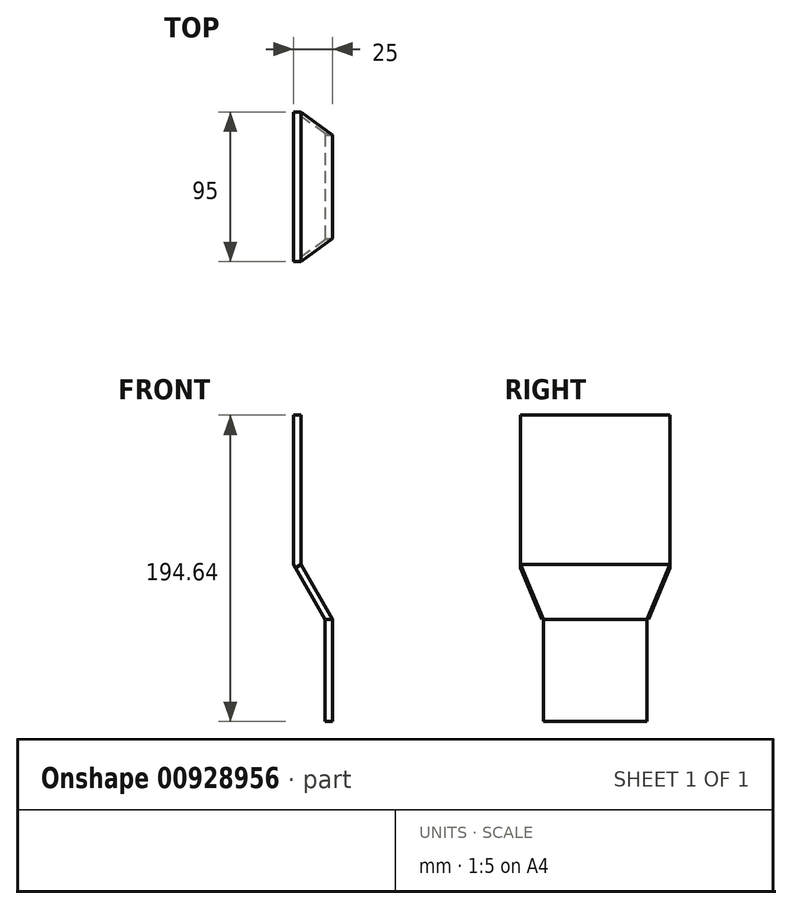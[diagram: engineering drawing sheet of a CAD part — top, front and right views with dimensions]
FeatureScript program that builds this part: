
annotation { "Feature Type Name" : "Feature", "Feature Type Description" : "" }
export const myFeature = defineFeature(function(context is Context, id is Id, definition is map)
    precondition{}
    {
        {
            var Q0;
            Q0=qCreatedBy(makeId("Right.planeOp"),FACE);
            var sketch = newSketch(context, id + "F0", { "sketchPlane" : qUnion([Q0])});
            skLineSegment(sketch, "E0.bottom", {"start": v(-47.5, 47.5) * mm, "end": v(47.5, 47.5) * mm});
            skLineSegment(sketch, "E0.top", {"start": v(-47.5, -47.5) * mm, "end": v(47.5, -47.5) * mm});
            skLineSegment(sketch, "E0.left", {"start": v(-47.5, 47.5) * mm, "end": v(-47.5, -47.5) * mm});
            skLineSegment(sketch, "E0.right", {"start": v(47.5, 47.5) * mm, "end": v(47.5, -47.5) * mm});
            skLineSegment(sketch, "E1", {"start": v(0, 83.18) * mm, "end": v(0, -90.06) * mm, "construction": true});
            skLineSegment(sketch, "E2", {"start": v(-68.56, 0) * mm, "end": v(78.45, 0) * mm, "construction": true});
            skSolve(sketch);
        }
        {
            var Q0;
            Q0 = qSketchRegion(id + "F0", true);
            extrude(context, id + "F1", {"entities" : qUnion([Q0]), "depth" : 5 * mm, "offsetDistance" : 25.4 * mm});
        }
        {
            var Q0;
            Q0=makeQuery(id+"F1.opExtrude","SWEPT_FACE",FACE,{"disambiguationData":[OSD([sQuery(id+"F0.wireOp",EDGE,"E0.left")])]});
            var sketch = newSketch(context, id + "F2", { "sketchPlane" : qUnion([Q0])});
            skLineSegment(sketch, "E3", {"start": v(5, -47.5) * mm, "end": v(25, -82.14) * mm});
            skLineSegment(sketch, "E4", {"start": v(0, -47.5) * mm, "end": v(5, -47.5) * mm});
            skLineSegment(sketch, "E5", {"start": v(0, -47.5) * mm, "end": v(20, -82.14) * mm});
            skLineSegment(sketch, "E6", {"start": v(20, -82.14) * mm, "end": v(25, -82.14) * mm});
            skLineSegment(sketch, "E7", {"start": v(20, -82.14) * mm, "end": v(20, -147.14) * mm});
            skLineSegment(sketch, "E8", {"start": v(20, -147.14) * mm, "end": v(25, -147.14) * mm});
            skLineSegment(sketch, "E9", {"start": v(25, -147.14) * mm, "end": v(25, -82.14) * mm});
            skSolve(sketch);
        }
        {
            var Q0;
            Q0 = qSketchRegion(id + "F2", true);
            var Q1;
            Q1=makeQuery(id+"F1.opExtrude","SWEPT_FACE",FACE,{"disambiguationData":[OSD([sQuery(id+"F0.wireOp",EDGE,"E0.right")])]});
            extrude(context, id + "F3", {"entities" : qUnion([Q0]), "operationType" : NewBodyOperationType.ADD, "endBound" : BoundingType.UP_TO_SURFACE, "oppositeDirection" : true, "depth" : 25.4 * mm, "endBoundEntityFace" : qUnion([Q1]), "offsetDistance" : 25.4 * mm});
        }
        {
            var Q0;
            Q0=makeQuery(id+"F3.opExtrude","SWEPT_FACE",FACE,{"disambiguationData":[OSD([sQuery(id+"F2.wireOp",EDGE,"E3")])]});
            var sketch = newSketch(context, id + "F4", { "sketchPlane" : qUnion([Q0])});
            skLineSegment(sketch, "E10", {"start": v(-47.5, -43.64) * mm, "end": v(-32.94, -83.64) * mm});
            skLineSegment(sketch, "E11", {"start": v(47.5, -43.64) * mm, "end": v(32.94, -83.64) * mm});
            skLineSegment(sketch, "E12", {"start": v(-32.94, -83.64) * mm, "end": v(-47.5, -83.64) * mm});
            skLineSegment(sketch, "E13", {"start": v(-47.5, -83.64) * mm, "end": v(-47.5, -43.64) * mm});
            skLineSegment(sketch, "E14", {"start": v(32.94, -83.64) * mm, "end": v(47.5, -83.64) * mm});
            skLineSegment(sketch, "E15", {"start": v(47.5, -83.64) * mm, "end": v(47.5, -43.64) * mm});
            skSolve(sketch);
        }
        {
            var Q0;
            Q0 = qSketchRegion(id + "F4", true);
            extrude(context, id + "F5", {"entities" : qUnion([Q0]), "operationType" : NewBodyOperationType.REMOVE, "oppositeDirection" : true, "depth" : 25.4 * mm, "offsetDistance" : 25.4 * mm});
        }
        {
            var Q0;
            Q0=makeQuery(id+"F3.opExtrude","SWEPT_FACE",FACE,{"disambiguationData":[OSD([sQuery(id+"F2.wireOp",EDGE,"E9")])]});
            var sketch = newSketch(context, id + "F6", { "sketchPlane" : qUnion([Q0])});
            skLineSegment(sketch, "E16", {"start": v(-47.5, -82.14) * mm, "end": v(-32.94, -82.14) * mm});
            skLineSegment(sketch, "E17", {"start": v(-32.94, -82.14) * mm, "end": v(-32.94, -147.14) * mm});
            skLineSegment(sketch, "E18", {"start": v(-32.94, -147.14) * mm, "end": v(-47.5, -147.14) * mm});
            skLineSegment(sketch, "E19", {"start": v(-47.5, -147.14) * mm, "end": v(-47.5, -82.14) * mm});
            skLineSegment(sketch, "E20", {"start": v(32.94, -82.14) * mm, "end": v(47.5, -82.14) * mm});
            skLineSegment(sketch, "E21", {"start": v(47.5, -82.14) * mm, "end": v(47.5, -147.14) * mm});
            skLineSegment(sketch, "E22", {"start": v(47.5, -147.14) * mm, "end": v(32.94, -147.14) * mm});
            skLineSegment(sketch, "E23", {"start": v(32.94, -147.14) * mm, "end": v(32.94, -82.14) * mm});
            skSolve(sketch);
        }
        {
            var Q0;
            Q0 = qSketchRegion(id + "F6", true);
            extrude(context, id + "F7", {"entities" : qUnion([Q0]), "operationType" : NewBodyOperationType.REMOVE, "oppositeDirection" : true, "depth" : 25.4 * mm, "offsetDistance" : 25.4 * mm});
        }
    });
